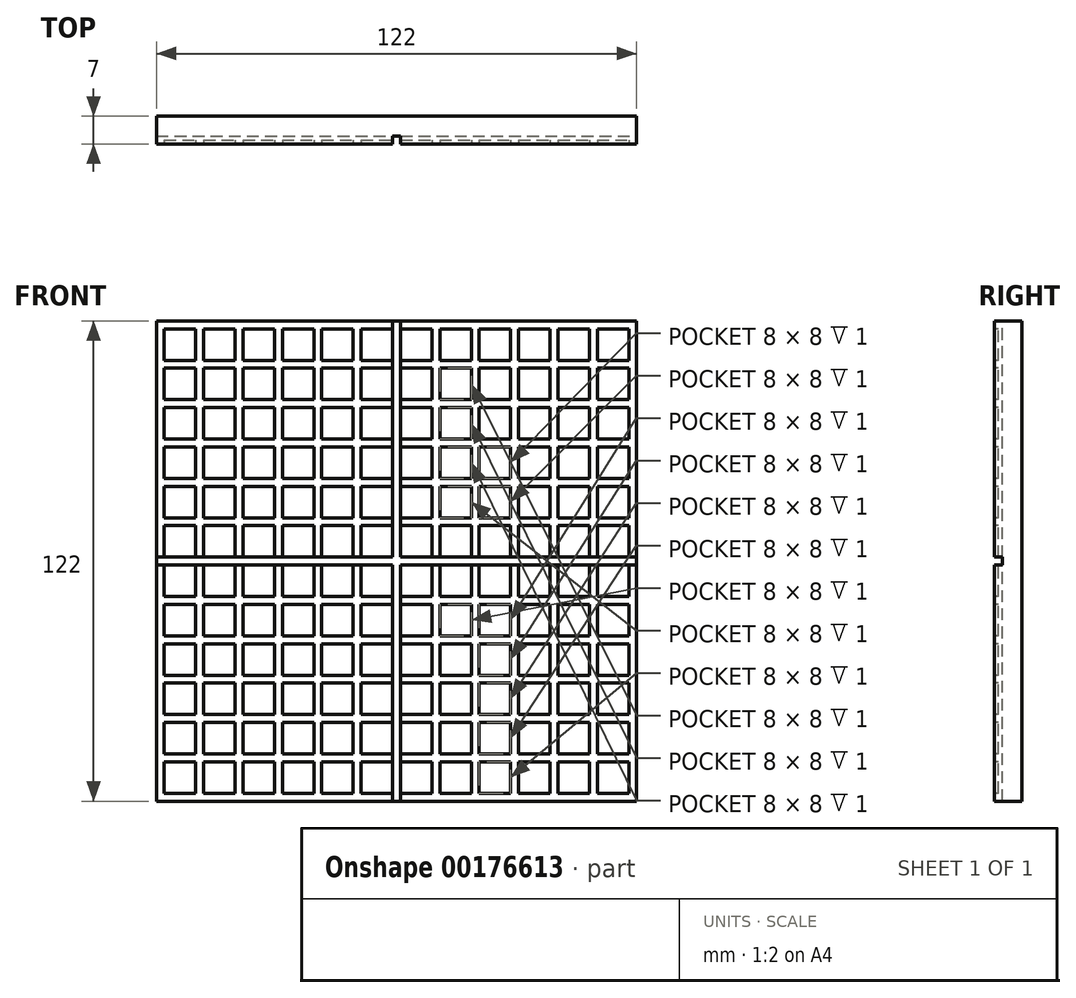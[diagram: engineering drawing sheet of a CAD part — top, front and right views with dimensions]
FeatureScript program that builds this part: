
annotation { "Feature Type Name" : "Feature", "Feature Type Description" : "" }
export const myFeature = defineFeature(function(context is Context, id is Id, definition is map)
    precondition{}
    {
        {
            var Q0;
            Q0=qCreatedBy(makeId("Front.planeOp"),FACE);
            var sketch = newSketch(context, id + "F0", { "sketchPlane" : qUnion([Q0])});
            skLineSegment(sketch, "E0.bottom", {"start": v(-61, 61) * mm, "end": v(61, 61) * mm});
            skLineSegment(sketch, "E0.top", {"start": v(-61, -61) * mm, "end": v(61, -61) * mm});
            skLineSegment(sketch, "E0.left", {"start": v(-61, 61) * mm, "end": v(-61, -61) * mm});
            skLineSegment(sketch, "E0.right", {"start": v(61, 61) * mm, "end": v(61, -61) * mm});
            skPoint(sketch, "E0.middle", {"position": v(0, 0) * mm});
            skSolve(sketch);
        }
        {
            var Q0;
            Q0=qCreatedBy(makeId("Front.planeOp"),FACE);
            var sketch = newSketch(context, id + "F1", { "sketchPlane" : qUnion([Q0])});
            skLineSegment(sketch, "E1.bottom", {"start": v(-61, 1) * mm, "end": v(61, 1) * mm});
            skLineSegment(sketch, "E1.top", {"start": v(-61, -1) * mm, "end": v(61, -1) * mm});
            skLineSegment(sketch, "E1.left", {"start": v(-61, 1) * mm, "end": v(-61, -1) * mm});
            skLineSegment(sketch, "E1.right", {"start": v(61, 1) * mm, "end": v(61, -1.62) * mm});
            skPoint(sketch, "E1.middle", {"position": v(0, 0) * mm});
            skLineSegment(sketch, "E2.bottom", {"start": v(-1, 61) * mm, "end": v(1, 61) * mm});
            skLineSegment(sketch, "E2.top", {"start": v(-1, -61) * mm, "end": v(1, -61) * mm});
            skLineSegment(sketch, "E2.left", {"start": v(-1, 61) * mm, "end": v(-1, -61) * mm});
            skLineSegment(sketch, "E2.right", {"start": v(1, 61) * mm, "end": v(1, -61) * mm});
            skSolve(sketch);
        }
        {
            var Q0;
            Q0=makeQuery(id+"F0.imprint","IMPRINT",FACE,{"disambiguationData":[TD([[makeQuery(id+"F0.imprint","IMPRINT",EDGE,{"derivedFrom":sQuery(id+"F0.wireOp",EDGE,"E0.bottom")}),-1.0]])]});
            var Q1;
            Q1 = qSketchRegion(id + "F4", true);
            extrude(context, id + "F2", {"entities" : qUnion([Q0, Q1]), "depth" : 7 * mm});
        }
        {
            var Q0;
            Q0 = qSketchRegion(id + "F1", true);
            extrude(context, id + "F3", {"entities" : qUnion([Q0]), "operationType" : NewBodyOperationType.ADD, "endBound" : BoundingType.UP_TO_NEXT, "depth" : 3 * mm, "offsetDistance" : 25 * mm});
        }
        {
            var Q0;
            {var subQ0=sQuery(id+"F1.wireOp",EDGE,"E1.left");var subQ1=sQuery(id+"F1.wireOp",EDGE,"E1.bottom");var subQ4=sQuery(id+"F0.wireOp",EDGE,"E0.left");var subQ5=sQuery(id+"F0.wireOp",EDGE,"E0.bottom");Q0=makeQuery(id+"F3.boolean.opBoolean","SPLIT",FACE,{"disambiguationData":[TD([makeQuery(id+"F3.opExtrude","SWEPT_FACE",FACE,{"disambiguationData":[OSD([subQ1]),TDD([makeQuery(id+"F1.imprint","IMPRINT",EDGE,{"disambiguationData":[TD([[makeQuery(id+"F1.imprint","INTERSECT",VERTEX,{"derivedFrom":[subQ1,subQ0]}),-1.0]])],"derivedFrom":subQ1})])]})])],"derivedFrom":makeQuery(id+"F2.opExtrude","CAP_FACE",FACE,{"disambiguationData":[OSD([subQ5,sQuery(id+"F0.wireOp",EDGE,"E0.top"),subQ4,sQuery(id+"F0.wireOp",EDGE,"E0.right")])],"isStart":false})});}
            var sketch = newSketch(context, id + "F4", { "sketchPlane" : qUnion([Q0])});
            skLineSegment(sketch, "E3.bottom", {"start": v(-59, -59) * mm, "end": v(-51, -59) * mm});
            skLineSegment(sketch, "E3.top", {"start": v(-59, -51) * mm, "end": v(-51, -51) * mm});
            skLineSegment(sketch, "E3.left", {"start": v(-59, -59) * mm, "end": v(-59, -51) * mm});
            skLineSegment(sketch, "E3.right", {"start": v(-51, -59) * mm, "end": v(-51, -51) * mm});
            skLineSegment(sketch, "E4.0.1.0", {"start": v(-51, -49) * mm, "end": v(-51, -41) * mm});
            skLineSegment(sketch, "E4.0.1.1", {"start": v(-59, -49) * mm, "end": v(-59, -41) * mm});
            skLineSegment(sketch, "E4.0.1.2", {"start": v(-59, -41) * mm, "end": v(-51, -41) * mm});
            skLineSegment(sketch, "E4.0.1.3", {"start": v(-59, -49) * mm, "end": v(-51, -49) * mm});
            skLineSegment(sketch, "E4.0.2.0", {"start": v(-51, -39) * mm, "end": v(-51, -31) * mm});
            skLineSegment(sketch, "E4.0.2.1", {"start": v(-59, -39) * mm, "end": v(-59, -31) * mm});
            skLineSegment(sketch, "E4.0.2.2", {"start": v(-59, -31) * mm, "end": v(-51, -31) * mm});
            skLineSegment(sketch, "E4.0.2.3", {"start": v(-59, -39) * mm, "end": v(-51, -39) * mm});
            skLineSegment(sketch, "E4.0.3.0", {"start": v(-51, -29) * mm, "end": v(-51, -21) * mm});
            skLineSegment(sketch, "E4.0.3.1", {"start": v(-59, -29) * mm, "end": v(-59, -21) * mm});
            skLineSegment(sketch, "E4.0.3.2", {"start": v(-59, -21) * mm, "end": v(-51, -21) * mm});
            skLineSegment(sketch, "E4.0.3.3", {"start": v(-59, -29) * mm, "end": v(-51, -29) * mm});
            skLineSegment(sketch, "E4.0.4.0", {"start": v(-51, -19) * mm, "end": v(-51, -11) * mm});
            skLineSegment(sketch, "E4.0.4.1", {"start": v(-59, -19) * mm, "end": v(-59, -11) * mm});
            skLineSegment(sketch, "E4.0.4.2", {"start": v(-59, -11) * mm, "end": v(-51, -11) * mm});
            skLineSegment(sketch, "E4.0.4.3", {"start": v(-59, -19) * mm, "end": v(-51, -19) * mm});
            skLineSegment(sketch, "E4.0.5.0", {"start": v(-51, -9) * mm, "end": v(-51, -1) * mm});
            skLineSegment(sketch, "E4.0.5.1", {"start": v(-59, -9) * mm, "end": v(-59, -1) * mm});
            skLineSegment(sketch, "E4.0.5.2", {"start": v(-59, -1) * mm, "end": v(-51, -1) * mm});
            skLineSegment(sketch, "E4.0.5.3", {"start": v(-59, -9) * mm, "end": v(-51, -9) * mm});
            skLineSegment(sketch, "E4.0.6.0", {"start": v(-51, 1) * mm, "end": v(-51, 9) * mm});
            skLineSegment(sketch, "E4.0.6.1", {"start": v(-59, 1) * mm, "end": v(-59, 9) * mm});
            skLineSegment(sketch, "E4.0.6.2", {"start": v(-59, 9) * mm, "end": v(-51, 9) * mm});
            skLineSegment(sketch, "E4.0.6.3", {"start": v(-59, 1) * mm, "end": v(-51, 1) * mm});
            skLineSegment(sketch, "E4.0.7.0", {"start": v(-51, 11) * mm, "end": v(-51, 19) * mm});
            skLineSegment(sketch, "E4.0.7.1", {"start": v(-59, 11) * mm, "end": v(-59, 19) * mm});
            skLineSegment(sketch, "E4.0.7.2", {"start": v(-59, 19) * mm, "end": v(-51, 19) * mm});
            skLineSegment(sketch, "E4.0.7.3", {"start": v(-59, 11) * mm, "end": v(-51, 11) * mm});
            skLineSegment(sketch, "E4.0.8.0", {"start": v(-51, 21) * mm, "end": v(-51, 29) * mm});
            skLineSegment(sketch, "E4.0.8.1", {"start": v(-59, 21) * mm, "end": v(-59, 29) * mm});
            skLineSegment(sketch, "E4.0.8.2", {"start": v(-59, 29) * mm, "end": v(-51, 29) * mm});
            skLineSegment(sketch, "E4.0.8.3", {"start": v(-59, 21) * mm, "end": v(-51, 21) * mm});
            skLineSegment(sketch, "E4.0.9.0", {"start": v(-51, 31) * mm, "end": v(-51, 39) * mm});
            skLineSegment(sketch, "E4.0.9.1", {"start": v(-59, 31) * mm, "end": v(-59, 39) * mm});
            skLineSegment(sketch, "E4.0.9.2", {"start": v(-59, 39) * mm, "end": v(-51, 39) * mm});
            skLineSegment(sketch, "E4.0.9.3", {"start": v(-59, 31) * mm, "end": v(-51, 31) * mm});
            skLineSegment(sketch, "E4.0.10.0", {"start": v(-51, 41) * mm, "end": v(-51, 49) * mm});
            skLineSegment(sketch, "E4.0.10.1", {"start": v(-59, 41) * mm, "end": v(-59, 49) * mm});
            skLineSegment(sketch, "E4.0.10.2", {"start": v(-59, 49) * mm, "end": v(-51, 49) * mm});
            skLineSegment(sketch, "E4.0.10.3", {"start": v(-59, 41) * mm, "end": v(-51, 41) * mm});
            skLineSegment(sketch, "E4.1.0.0", {"start": v(-41, -59) * mm, "end": v(-41, -51) * mm});
            skLineSegment(sketch, "E4.1.0.1", {"start": v(-49, -59) * mm, "end": v(-49, -51) * mm});
            skLineSegment(sketch, "E4.1.0.2", {"start": v(-49, -51) * mm, "end": v(-41, -51) * mm});
            skLineSegment(sketch, "E4.1.0.3", {"start": v(-49, -59) * mm, "end": v(-41, -59) * mm});
            skLineSegment(sketch, "E4.1.1.0", {"start": v(-41, -49) * mm, "end": v(-41, -41) * mm});
            skLineSegment(sketch, "E4.1.1.1", {"start": v(-49, -49) * mm, "end": v(-49, -41) * mm});
            skLineSegment(sketch, "E4.1.1.2", {"start": v(-49, -41) * mm, "end": v(-41, -41) * mm});
            skLineSegment(sketch, "E4.1.1.3", {"start": v(-49, -49) * mm, "end": v(-41, -49) * mm});
            skLineSegment(sketch, "E4.1.2.0", {"start": v(-41, -39) * mm, "end": v(-41, -31) * mm});
            skLineSegment(sketch, "E4.1.2.1", {"start": v(-49, -39) * mm, "end": v(-49, -31) * mm});
            skLineSegment(sketch, "E4.1.2.2", {"start": v(-49, -31) * mm, "end": v(-41, -31) * mm});
            skLineSegment(sketch, "E4.1.2.3", {"start": v(-49, -39) * mm, "end": v(-41, -39) * mm});
            skLineSegment(sketch, "E4.1.3.0", {"start": v(-41, -29) * mm, "end": v(-41, -21) * mm});
            skLineSegment(sketch, "E4.1.3.1", {"start": v(-49, -29) * mm, "end": v(-49, -21) * mm});
            skLineSegment(sketch, "E4.1.3.2", {"start": v(-49, -21) * mm, "end": v(-41, -21) * mm});
            skLineSegment(sketch, "E4.1.3.3", {"start": v(-49, -29) * mm, "end": v(-41, -29) * mm});
            skLineSegment(sketch, "E4.1.4.0", {"start": v(-41, -19) * mm, "end": v(-41, -11) * mm});
            skLineSegment(sketch, "E4.1.4.1", {"start": v(-49, -19) * mm, "end": v(-49, -11) * mm});
            skLineSegment(sketch, "E4.1.4.2", {"start": v(-49, -11) * mm, "end": v(-41, -11) * mm});
            skLineSegment(sketch, "E4.1.4.3", {"start": v(-49, -19) * mm, "end": v(-41, -19) * mm});
            skLineSegment(sketch, "E4.1.5.0", {"start": v(-41, -9) * mm, "end": v(-41, -1) * mm});
            skLineSegment(sketch, "E4.1.5.1", {"start": v(-49, -9) * mm, "end": v(-49, -1) * mm});
            skLineSegment(sketch, "E4.1.5.2", {"start": v(-49, -1) * mm, "end": v(-41, -1) * mm});
            skLineSegment(sketch, "E4.1.5.3", {"start": v(-49, -9) * mm, "end": v(-41, -9) * mm});
            skLineSegment(sketch, "E4.1.6.0", {"start": v(-41, 1) * mm, "end": v(-41, 9) * mm});
            skLineSegment(sketch, "E4.1.6.1", {"start": v(-49, 1) * mm, "end": v(-49, 9) * mm});
            skLineSegment(sketch, "E4.1.6.2", {"start": v(-49, 9) * mm, "end": v(-41, 9) * mm});
            skLineSegment(sketch, "E4.1.6.3", {"start": v(-49, 1) * mm, "end": v(-41, 1) * mm});
            skLineSegment(sketch, "E4.1.7.0", {"start": v(-41, 11) * mm, "end": v(-41, 19) * mm});
            skLineSegment(sketch, "E4.1.7.1", {"start": v(-49, 11) * mm, "end": v(-49, 19) * mm});
            skLineSegment(sketch, "E4.1.7.2", {"start": v(-49, 19) * mm, "end": v(-41, 19) * mm});
            skLineSegment(sketch, "E4.1.7.3", {"start": v(-49, 11) * mm, "end": v(-41, 11) * mm});
            skLineSegment(sketch, "E4.1.8.0", {"start": v(-41, 21) * mm, "end": v(-41, 29) * mm});
            skLineSegment(sketch, "E4.1.8.1", {"start": v(-49, 21) * mm, "end": v(-49, 29) * mm});
            skLineSegment(sketch, "E4.1.8.2", {"start": v(-49, 29) * mm, "end": v(-41, 29) * mm});
            skLineSegment(sketch, "E4.1.8.3", {"start": v(-49, 21) * mm, "end": v(-41, 21) * mm});
            skLineSegment(sketch, "E4.1.9.0", {"start": v(-41, 31) * mm, "end": v(-41, 39) * mm});
            skLineSegment(sketch, "E4.1.9.1", {"start": v(-49, 31) * mm, "end": v(-49, 39) * mm});
            skLineSegment(sketch, "E4.1.9.2", {"start": v(-49, 39) * mm, "end": v(-41, 39) * mm});
            skLineSegment(sketch, "E4.1.9.3", {"start": v(-49, 31) * mm, "end": v(-41, 31) * mm});
            skLineSegment(sketch, "E4.1.10.0", {"start": v(-41, 41) * mm, "end": v(-41, 49) * mm});
            skLineSegment(sketch, "E4.1.10.1", {"start": v(-49, 41) * mm, "end": v(-49, 49) * mm});
            skLineSegment(sketch, "E4.1.10.2", {"start": v(-49, 49) * mm, "end": v(-41, 49) * mm});
            skLineSegment(sketch, "E4.1.10.3", {"start": v(-49, 41) * mm, "end": v(-41, 41) * mm});
            skLineSegment(sketch, "E4.2.0.0", {"start": v(-31, -59) * mm, "end": v(-31, -51) * mm});
            skLineSegment(sketch, "E4.2.0.1", {"start": v(-39, -59) * mm, "end": v(-39, -51) * mm});
            skLineSegment(sketch, "E4.2.0.2", {"start": v(-39, -51) * mm, "end": v(-31, -51) * mm});
            skLineSegment(sketch, "E4.2.0.3", {"start": v(-39, -59) * mm, "end": v(-31, -59) * mm});
            skLineSegment(sketch, "E4.2.1.0", {"start": v(-31, -49) * mm, "end": v(-31, -41) * mm});
            skLineSegment(sketch, "E4.2.1.1", {"start": v(-39, -49) * mm, "end": v(-39, -41) * mm});
            skLineSegment(sketch, "E4.2.1.2", {"start": v(-39, -41) * mm, "end": v(-31, -41) * mm});
            skLineSegment(sketch, "E4.2.1.3", {"start": v(-39, -49) * mm, "end": v(-31, -49) * mm});
            skLineSegment(sketch, "E4.2.2.0", {"start": v(-31, -39) * mm, "end": v(-31, -31) * mm});
            skLineSegment(sketch, "E4.2.2.1", {"start": v(-39, -39) * mm, "end": v(-39, -31) * mm});
            skLineSegment(sketch, "E4.2.2.2", {"start": v(-39, -31) * mm, "end": v(-31, -31) * mm});
            skLineSegment(sketch, "E4.2.2.3", {"start": v(-39, -39) * mm, "end": v(-31, -39) * mm});
            skLineSegment(sketch, "E4.2.3.0", {"start": v(-31, -29) * mm, "end": v(-31, -21) * mm});
            skLineSegment(sketch, "E4.2.3.1", {"start": v(-39, -29) * mm, "end": v(-39, -21) * mm});
            skLineSegment(sketch, "E4.2.3.2", {"start": v(-39, -21) * mm, "end": v(-31, -21) * mm});
            skLineSegment(sketch, "E4.2.3.3", {"start": v(-39, -29) * mm, "end": v(-31, -29) * mm});
            skLineSegment(sketch, "E4.2.4.0", {"start": v(-31, -19) * mm, "end": v(-31, -11) * mm});
            skLineSegment(sketch, "E4.2.4.1", {"start": v(-39, -19) * mm, "end": v(-39, -11) * mm});
            skLineSegment(sketch, "E4.2.4.2", {"start": v(-39, -11) * mm, "end": v(-31, -11) * mm});
            skLineSegment(sketch, "E4.2.4.3", {"start": v(-39, -19) * mm, "end": v(-31, -19) * mm});
            skLineSegment(sketch, "E4.2.5.0", {"start": v(-31, -9) * mm, "end": v(-31, -1) * mm});
            skLineSegment(sketch, "E4.2.5.1", {"start": v(-39, -9) * mm, "end": v(-39, -1) * mm});
            skLineSegment(sketch, "E4.2.5.2", {"start": v(-39, -1) * mm, "end": v(-31, -1) * mm});
            skLineSegment(sketch, "E4.2.5.3", {"start": v(-39, -9) * mm, "end": v(-31, -9) * mm});
            skLineSegment(sketch, "E4.2.6.0", {"start": v(-31, 1) * mm, "end": v(-31, 9) * mm});
            skLineSegment(sketch, "E4.2.6.1", {"start": v(-39, 1) * mm, "end": v(-39, 9) * mm});
            skLineSegment(sketch, "E4.2.6.2", {"start": v(-39, 9) * mm, "end": v(-31, 9) * mm});
            skLineSegment(sketch, "E4.2.6.3", {"start": v(-39, 1) * mm, "end": v(-31, 1) * mm});
            skLineSegment(sketch, "E4.2.7.0", {"start": v(-31, 11) * mm, "end": v(-31, 19) * mm});
            skLineSegment(sketch, "E4.2.7.1", {"start": v(-39, 11) * mm, "end": v(-39, 19) * mm});
            skLineSegment(sketch, "E4.2.7.2", {"start": v(-39, 19) * mm, "end": v(-31, 19) * mm});
            skLineSegment(sketch, "E4.2.7.3", {"start": v(-39, 11) * mm, "end": v(-31, 11) * mm});
            skLineSegment(sketch, "E4.2.8.0", {"start": v(-31, 21) * mm, "end": v(-31, 29) * mm});
            skLineSegment(sketch, "E4.2.8.1", {"start": v(-39, 21) * mm, "end": v(-39, 29) * mm});
            skLineSegment(sketch, "E4.2.8.2", {"start": v(-39, 29) * mm, "end": v(-31, 29) * mm});
            skLineSegment(sketch, "E4.2.8.3", {"start": v(-39, 21) * mm, "end": v(-31, 21) * mm});
            skLineSegment(sketch, "E4.2.9.0", {"start": v(-31, 31) * mm, "end": v(-31, 39) * mm});
            skLineSegment(sketch, "E4.2.9.1", {"start": v(-39, 31) * mm, "end": v(-39, 39) * mm});
            skLineSegment(sketch, "E4.2.9.2", {"start": v(-39, 39) * mm, "end": v(-31, 39) * mm});
            skLineSegment(sketch, "E4.2.9.3", {"start": v(-39, 31) * mm, "end": v(-31, 31) * mm});
            skLineSegment(sketch, "E4.2.10.0", {"start": v(-31, 41) * mm, "end": v(-31, 49) * mm});
            skLineSegment(sketch, "E4.2.10.1", {"start": v(-39, 41) * mm, "end": v(-39, 49) * mm});
            skLineSegment(sketch, "E4.2.10.2", {"start": v(-39, 49) * mm, "end": v(-31, 49) * mm});
            skLineSegment(sketch, "E4.2.10.3", {"start": v(-39, 41) * mm, "end": v(-31, 41) * mm});
            skLineSegment(sketch, "E4.3.0.0", {"start": v(-21, -59) * mm, "end": v(-21, -51) * mm});
            skLineSegment(sketch, "E4.3.0.1", {"start": v(-29, -59) * mm, "end": v(-29, -51) * mm});
            skLineSegment(sketch, "E4.3.0.2", {"start": v(-29, -51) * mm, "end": v(-21, -51) * mm});
            skLineSegment(sketch, "E4.3.0.3", {"start": v(-29, -59) * mm, "end": v(-21, -59) * mm});
            skLineSegment(sketch, "E4.3.1.0", {"start": v(-21, -49) * mm, "end": v(-21, -41) * mm});
            skLineSegment(sketch, "E4.3.1.1", {"start": v(-29, -49) * mm, "end": v(-29, -41) * mm});
            skLineSegment(sketch, "E4.3.1.2", {"start": v(-29, -41) * mm, "end": v(-21, -41) * mm});
            skLineSegment(sketch, "E4.3.1.3", {"start": v(-29, -49) * mm, "end": v(-21, -49) * mm});
            skLineSegment(sketch, "E4.3.2.0", {"start": v(-21, -39) * mm, "end": v(-21, -31) * mm});
            skLineSegment(sketch, "E4.3.2.1", {"start": v(-29, -39) * mm, "end": v(-29, -31) * mm});
            skLineSegment(sketch, "E4.3.2.2", {"start": v(-29, -31) * mm, "end": v(-21, -31) * mm});
            skLineSegment(sketch, "E4.3.2.3", {"start": v(-29, -39) * mm, "end": v(-21, -39) * mm});
            skLineSegment(sketch, "E4.3.3.0", {"start": v(-21, -29) * mm, "end": v(-21, -21) * mm});
            skLineSegment(sketch, "E4.3.3.1", {"start": v(-29, -29) * mm, "end": v(-29, -21) * mm});
            skLineSegment(sketch, "E4.3.3.2", {"start": v(-29, -21) * mm, "end": v(-21, -21) * mm});
            skLineSegment(sketch, "E4.3.3.3", {"start": v(-29, -29) * mm, "end": v(-21, -29) * mm});
            skLineSegment(sketch, "E4.3.4.0", {"start": v(-21, -19) * mm, "end": v(-21, -11) * mm});
            skLineSegment(sketch, "E4.3.4.1", {"start": v(-29, -19) * mm, "end": v(-29, -11) * mm});
            skLineSegment(sketch, "E4.3.4.2", {"start": v(-29, -11) * mm, "end": v(-21, -11) * mm});
            skLineSegment(sketch, "E4.3.4.3", {"start": v(-29, -19) * mm, "end": v(-21, -19) * mm});
            skLineSegment(sketch, "E4.3.5.0", {"start": v(-21, -9) * mm, "end": v(-21, -1) * mm});
            skLineSegment(sketch, "E4.3.5.1", {"start": v(-29, -9) * mm, "end": v(-29, -1) * mm});
            skLineSegment(sketch, "E4.3.5.2", {"start": v(-29, -1) * mm, "end": v(-21, -1) * mm});
            skLineSegment(sketch, "E4.3.5.3", {"start": v(-29, -9) * mm, "end": v(-21, -9) * mm});
            skLineSegment(sketch, "E4.3.6.0", {"start": v(-21, 1) * mm, "end": v(-21, 9) * mm});
            skLineSegment(sketch, "E4.3.6.1", {"start": v(-29, 1) * mm, "end": v(-29, 9) * mm});
            skLineSegment(sketch, "E4.3.6.2", {"start": v(-29, 9) * mm, "end": v(-21, 9) * mm});
            skLineSegment(sketch, "E4.3.6.3", {"start": v(-29, 1) * mm, "end": v(-21, 1) * mm});
            skLineSegment(sketch, "E4.3.7.0", {"start": v(-21, 11) * mm, "end": v(-21, 19) * mm});
            skLineSegment(sketch, "E4.3.7.1", {"start": v(-29, 11) * mm, "end": v(-29, 19) * mm});
            skLineSegment(sketch, "E4.3.7.2", {"start": v(-29, 19) * mm, "end": v(-21, 19) * mm});
            skLineSegment(sketch, "E4.3.7.3", {"start": v(-29, 11) * mm, "end": v(-21, 11) * mm});
            skLineSegment(sketch, "E4.3.8.0", {"start": v(-21, 21) * mm, "end": v(-21, 29) * mm});
            skLineSegment(sketch, "E4.3.8.1", {"start": v(-29, 21) * mm, "end": v(-29, 29) * mm});
            skLineSegment(sketch, "E4.3.8.2", {"start": v(-29, 29) * mm, "end": v(-21, 29) * mm});
            skLineSegment(sketch, "E4.3.8.3", {"start": v(-29, 21) * mm, "end": v(-21, 21) * mm});
            skLineSegment(sketch, "E4.3.9.0", {"start": v(-21, 31) * mm, "end": v(-21, 39) * mm});
            skLineSegment(sketch, "E4.3.9.1", {"start": v(-29, 31) * mm, "end": v(-29, 39) * mm});
            skLineSegment(sketch, "E4.3.9.2", {"start": v(-29, 39) * mm, "end": v(-21, 39) * mm});
            skLineSegment(sketch, "E4.3.9.3", {"start": v(-29, 31) * mm, "end": v(-21, 31) * mm});
            skLineSegment(sketch, "E4.3.10.0", {"start": v(-21, 41) * mm, "end": v(-21, 49) * mm});
            skLineSegment(sketch, "E4.3.10.1", {"start": v(-29, 41) * mm, "end": v(-29, 49) * mm});
            skLineSegment(sketch, "E4.3.10.2", {"start": v(-29, 49) * mm, "end": v(-21, 49) * mm});
            skLineSegment(sketch, "E4.3.10.3", {"start": v(-29, 41) * mm, "end": v(-21, 41) * mm});
            skLineSegment(sketch, "E4.4.0.0", {"start": v(-11, -59) * mm, "end": v(-11, -51) * mm});
            skLineSegment(sketch, "E4.4.0.1", {"start": v(-19, -59) * mm, "end": v(-19, -51) * mm});
            skLineSegment(sketch, "E4.4.0.2", {"start": v(-19, -51) * mm, "end": v(-11, -51) * mm});
            skLineSegment(sketch, "E4.4.0.3", {"start": v(-19, -59) * mm, "end": v(-11, -59) * mm});
            skLineSegment(sketch, "E4.4.1.0", {"start": v(-11, -49) * mm, "end": v(-11, -41) * mm});
            skLineSegment(sketch, "E4.4.1.1", {"start": v(-19, -49) * mm, "end": v(-19, -41) * mm});
            skLineSegment(sketch, "E4.4.1.2", {"start": v(-19, -41) * mm, "end": v(-11, -41) * mm});
            skLineSegment(sketch, "E4.4.1.3", {"start": v(-19, -49) * mm, "end": v(-11, -49) * mm});
            skLineSegment(sketch, "E4.4.2.0", {"start": v(-11, -39) * mm, "end": v(-11, -31) * mm});
            skLineSegment(sketch, "E4.4.2.1", {"start": v(-19, -39) * mm, "end": v(-19, -31) * mm});
            skLineSegment(sketch, "E4.4.2.2", {"start": v(-19, -31) * mm, "end": v(-11, -31) * mm});
            skLineSegment(sketch, "E4.4.2.3", {"start": v(-19, -39) * mm, "end": v(-11, -39) * mm});
            skLineSegment(sketch, "E4.4.3.0", {"start": v(-11, -29) * mm, "end": v(-11, -21) * mm});
            skLineSegment(sketch, "E4.4.3.1", {"start": v(-19, -29) * mm, "end": v(-19, -21) * mm});
            skLineSegment(sketch, "E4.4.3.2", {"start": v(-19, -21) * mm, "end": v(-11, -21) * mm});
            skLineSegment(sketch, "E4.4.3.3", {"start": v(-19, -29) * mm, "end": v(-11, -29) * mm});
            skLineSegment(sketch, "E4.4.4.0", {"start": v(-11, -19) * mm, "end": v(-11, -11) * mm});
            skLineSegment(sketch, "E4.4.4.1", {"start": v(-19, -19) * mm, "end": v(-19, -11) * mm});
            skLineSegment(sketch, "E4.4.4.2", {"start": v(-19, -11) * mm, "end": v(-11, -11) * mm});
            skLineSegment(sketch, "E4.4.4.3", {"start": v(-19, -19) * mm, "end": v(-11, -19) * mm});
            skLineSegment(sketch, "E4.4.5.0", {"start": v(-11, -9) * mm, "end": v(-11, -1) * mm});
            skLineSegment(sketch, "E4.4.5.1", {"start": v(-19, -9) * mm, "end": v(-19, -1) * mm});
            skLineSegment(sketch, "E4.4.5.2", {"start": v(-19, -1) * mm, "end": v(-11, -1) * mm});
            skLineSegment(sketch, "E4.4.5.3", {"start": v(-19, -9) * mm, "end": v(-11, -9) * mm});
            skLineSegment(sketch, "E4.4.6.0", {"start": v(-11, 1) * mm, "end": v(-11, 9) * mm});
            skLineSegment(sketch, "E4.4.6.1", {"start": v(-19, 1) * mm, "end": v(-19, 9) * mm});
            skLineSegment(sketch, "E4.4.6.2", {"start": v(-19, 9) * mm, "end": v(-11, 9) * mm});
            skLineSegment(sketch, "E4.4.6.3", {"start": v(-19, 1) * mm, "end": v(-11, 1) * mm});
            skLineSegment(sketch, "E4.4.7.0", {"start": v(-11, 11) * mm, "end": v(-11, 19) * mm});
            skLineSegment(sketch, "E4.4.7.1", {"start": v(-19, 11) * mm, "end": v(-19, 19) * mm});
            skLineSegment(sketch, "E4.4.7.2", {"start": v(-19, 19) * mm, "end": v(-11, 19) * mm});
            skLineSegment(sketch, "E4.4.7.3", {"start": v(-19, 11) * mm, "end": v(-11, 11) * mm});
            skLineSegment(sketch, "E4.4.8.0", {"start": v(-11, 21) * mm, "end": v(-11, 29) * mm});
            skLineSegment(sketch, "E4.4.8.1", {"start": v(-19, 21) * mm, "end": v(-19, 29) * mm});
            skLineSegment(sketch, "E4.4.8.2", {"start": v(-19, 29) * mm, "end": v(-11, 29) * mm});
            skLineSegment(sketch, "E4.4.8.3", {"start": v(-19, 21) * mm, "end": v(-11, 21) * mm});
            skLineSegment(sketch, "E4.4.9.0", {"start": v(-11, 31) * mm, "end": v(-11, 39) * mm});
            skLineSegment(sketch, "E4.4.9.1", {"start": v(-19, 31) * mm, "end": v(-19, 39) * mm});
            skLineSegment(sketch, "E4.4.9.2", {"start": v(-19, 39) * mm, "end": v(-11, 39) * mm});
            skLineSegment(sketch, "E4.4.9.3", {"start": v(-19, 31) * mm, "end": v(-11, 31) * mm});
            skLineSegment(sketch, "E4.4.10.0", {"start": v(-11, 41) * mm, "end": v(-11, 49) * mm});
            skLineSegment(sketch, "E4.4.10.1", {"start": v(-19, 41) * mm, "end": v(-19, 49) * mm});
            skLineSegment(sketch, "E4.4.10.2", {"start": v(-19, 49) * mm, "end": v(-11, 49) * mm});
            skLineSegment(sketch, "E4.4.10.3", {"start": v(-19, 41) * mm, "end": v(-11, 41) * mm});
            skLineSegment(sketch, "E4.5.0.0", {"start": v(-1, -59) * mm, "end": v(-1, -51) * mm});
            skLineSegment(sketch, "E4.5.0.1", {"start": v(-9, -59) * mm, "end": v(-9, -51) * mm});
            skLineSegment(sketch, "E4.5.0.2", {"start": v(-9, -51) * mm, "end": v(-1, -51) * mm});
            skLineSegment(sketch, "E4.5.0.3", {"start": v(-9, -59) * mm, "end": v(-1, -59) * mm});
            skLineSegment(sketch, "E4.5.1.0", {"start": v(-1, -49) * mm, "end": v(-1, -41) * mm});
            skLineSegment(sketch, "E4.5.1.1", {"start": v(-9, -49) * mm, "end": v(-9, -41) * mm});
            skLineSegment(sketch, "E4.5.1.2", {"start": v(-9, -41) * mm, "end": v(-1, -41) * mm});
            skLineSegment(sketch, "E4.5.1.3", {"start": v(-9, -49) * mm, "end": v(-1, -49) * mm});
            skLineSegment(sketch, "E4.5.2.0", {"start": v(-1, -39) * mm, "end": v(-1, -31) * mm});
            skLineSegment(sketch, "E4.5.2.1", {"start": v(-9, -39) * mm, "end": v(-9, -31) * mm});
            skLineSegment(sketch, "E4.5.2.2", {"start": v(-9, -31) * mm, "end": v(-1, -31) * mm});
            skLineSegment(sketch, "E4.5.2.3", {"start": v(-9, -39) * mm, "end": v(-1, -39) * mm});
            skLineSegment(sketch, "E4.5.3.0", {"start": v(-1, -29) * mm, "end": v(-1, -21) * mm});
            skLineSegment(sketch, "E4.5.3.1", {"start": v(-9, -29) * mm, "end": v(-9, -21) * mm});
            skLineSegment(sketch, "E4.5.3.2", {"start": v(-9, -21) * mm, "end": v(-1, -21) * mm});
            skLineSegment(sketch, "E4.5.3.3", {"start": v(-9, -29) * mm, "end": v(-1, -29) * mm});
            skLineSegment(sketch, "E4.5.4.0", {"start": v(-1, -19) * mm, "end": v(-1, -11) * mm});
            skLineSegment(sketch, "E4.5.4.1", {"start": v(-9, -19) * mm, "end": v(-9, -11) * mm});
            skLineSegment(sketch, "E4.5.4.2", {"start": v(-9, -11) * mm, "end": v(-1, -11) * mm});
            skLineSegment(sketch, "E4.5.4.3", {"start": v(-9, -19) * mm, "end": v(-1, -19) * mm});
            skLineSegment(sketch, "E4.5.5.0", {"start": v(-1, -9) * mm, "end": v(-1, -1) * mm});
            skLineSegment(sketch, "E4.5.5.1", {"start": v(-9, -9) * mm, "end": v(-9, -1) * mm});
            skLineSegment(sketch, "E4.5.5.2", {"start": v(-9, -1) * mm, "end": v(-1, -1) * mm});
            skLineSegment(sketch, "E4.5.5.3", {"start": v(-9, -9) * mm, "end": v(-1, -9) * mm});
            skLineSegment(sketch, "E4.5.6.0", {"start": v(-1, 1) * mm, "end": v(-1, 9) * mm});
            skLineSegment(sketch, "E4.5.6.1", {"start": v(-9, 1) * mm, "end": v(-9, 9) * mm});
            skLineSegment(sketch, "E4.5.6.2", {"start": v(-9, 9) * mm, "end": v(-1, 9) * mm});
            skLineSegment(sketch, "E4.5.6.3", {"start": v(-9, 1) * mm, "end": v(-1, 1) * mm});
            skLineSegment(sketch, "E4.5.7.0", {"start": v(-1, 11) * mm, "end": v(-1, 19) * mm});
            skLineSegment(sketch, "E4.5.7.1", {"start": v(-9, 11) * mm, "end": v(-9, 19) * mm});
            skLineSegment(sketch, "E4.5.7.2", {"start": v(-9, 19) * mm, "end": v(-1, 19) * mm});
            skLineSegment(sketch, "E4.5.7.3", {"start": v(-9, 11) * mm, "end": v(-1, 11) * mm});
            skLineSegment(sketch, "E4.5.8.0", {"start": v(-1, 21) * mm, "end": v(-1, 29) * mm});
            skLineSegment(sketch, "E4.5.8.1", {"start": v(-9, 21) * mm, "end": v(-9, 29) * mm});
            skLineSegment(sketch, "E4.5.8.2", {"start": v(-9, 29) * mm, "end": v(-1, 29) * mm});
            skLineSegment(sketch, "E4.5.8.3", {"start": v(-9, 21) * mm, "end": v(-1, 21) * mm});
            skLineSegment(sketch, "E4.5.9.0", {"start": v(-1, 31) * mm, "end": v(-1, 39) * mm});
            skLineSegment(sketch, "E4.5.9.1", {"start": v(-9, 31) * mm, "end": v(-9, 39) * mm});
            skLineSegment(sketch, "E4.5.9.2", {"start": v(-9, 39) * mm, "end": v(-1, 39) * mm});
            skLineSegment(sketch, "E4.5.9.3", {"start": v(-9, 31) * mm, "end": v(-1, 31) * mm});
            skLineSegment(sketch, "E4.5.10.0", {"start": v(-1, 41) * mm, "end": v(-1, 49) * mm});
            skLineSegment(sketch, "E4.5.10.1", {"start": v(-9, 41) * mm, "end": v(-9, 49) * mm});
            skLineSegment(sketch, "E4.5.10.2", {"start": v(-9, 49) * mm, "end": v(-1, 49) * mm});
            skLineSegment(sketch, "E4.5.10.3", {"start": v(-9, 41) * mm, "end": v(-1, 41) * mm});
            skLineSegment(sketch, "E4.6.0.0", {"start": v(9, -59) * mm, "end": v(9, -51) * mm});
            skLineSegment(sketch, "E4.6.0.1", {"start": v(1, -59) * mm, "end": v(1, -51) * mm});
            skLineSegment(sketch, "E4.6.0.2", {"start": v(1, -51) * mm, "end": v(9, -51) * mm});
            skLineSegment(sketch, "E4.6.0.3", {"start": v(1, -59) * mm, "end": v(9, -59) * mm});
            skLineSegment(sketch, "E4.6.1.0", {"start": v(9, -49) * mm, "end": v(9, -41) * mm});
            skLineSegment(sketch, "E4.6.1.1", {"start": v(1, -49) * mm, "end": v(1, -41) * mm});
            skLineSegment(sketch, "E4.6.1.2", {"start": v(1, -41) * mm, "end": v(9, -41) * mm});
            skLineSegment(sketch, "E4.6.1.3", {"start": v(1, -49) * mm, "end": v(9, -49) * mm});
            skLineSegment(sketch, "E4.6.2.0", {"start": v(9, -39) * mm, "end": v(9, -31) * mm});
            skLineSegment(sketch, "E4.6.2.1", {"start": v(1, -39) * mm, "end": v(1, -31) * mm});
            skLineSegment(sketch, "E4.6.2.2", {"start": v(1, -31) * mm, "end": v(9, -31) * mm});
            skLineSegment(sketch, "E4.6.2.3", {"start": v(1, -39) * mm, "end": v(9, -39) * mm});
            skLineSegment(sketch, "E4.6.3.0", {"start": v(9, -29) * mm, "end": v(9, -21) * mm});
            skLineSegment(sketch, "E4.6.3.1", {"start": v(1, -29) * mm, "end": v(1, -21) * mm});
            skLineSegment(sketch, "E4.6.3.2", {"start": v(1, -21) * mm, "end": v(9, -21) * mm});
            skLineSegment(sketch, "E4.6.3.3", {"start": v(1, -29) * mm, "end": v(9, -29) * mm});
            skLineSegment(sketch, "E4.6.4.0", {"start": v(9, -19) * mm, "end": v(9, -11) * mm});
            skLineSegment(sketch, "E4.6.4.1", {"start": v(1, -19) * mm, "end": v(1, -11) * mm});
            skLineSegment(sketch, "E4.6.4.2", {"start": v(1, -11) * mm, "end": v(9, -11) * mm});
            skLineSegment(sketch, "E4.6.4.3", {"start": v(1, -19) * mm, "end": v(9, -19) * mm});
            skLineSegment(sketch, "E4.6.5.0", {"start": v(9, -9) * mm, "end": v(9, -1) * mm});
            skLineSegment(sketch, "E4.6.5.1", {"start": v(1, -9) * mm, "end": v(1, -1) * mm});
            skLineSegment(sketch, "E4.6.5.2", {"start": v(1, -1) * mm, "end": v(9, -1) * mm});
            skLineSegment(sketch, "E4.6.5.3", {"start": v(1, -9) * mm, "end": v(9, -9) * mm});
            skLineSegment(sketch, "E4.6.6.0", {"start": v(9, 1) * mm, "end": v(9, 9) * mm});
            skLineSegment(sketch, "E4.6.6.1", {"start": v(1, 1) * mm, "end": v(1, 9) * mm});
            skLineSegment(sketch, "E4.6.6.2", {"start": v(1, 9) * mm, "end": v(9, 9) * mm});
            skLineSegment(sketch, "E4.6.6.3", {"start": v(1, 1) * mm, "end": v(9, 1) * mm});
            skLineSegment(sketch, "E4.6.7.0", {"start": v(9, 11) * mm, "end": v(9, 19) * mm});
            skLineSegment(sketch, "E4.6.7.1", {"start": v(1, 11) * mm, "end": v(1, 19) * mm});
            skLineSegment(sketch, "E4.6.7.2", {"start": v(1, 19) * mm, "end": v(9, 19) * mm});
            skLineSegment(sketch, "E4.6.7.3", {"start": v(1, 11) * mm, "end": v(9, 11) * mm});
            skLineSegment(sketch, "E4.6.8.0", {"start": v(9, 21) * mm, "end": v(9, 29) * mm});
            skLineSegment(sketch, "E4.6.8.1", {"start": v(1, 21) * mm, "end": v(1, 29) * mm});
            skLineSegment(sketch, "E4.6.8.2", {"start": v(1, 29) * mm, "end": v(9, 29) * mm});
            skLineSegment(sketch, "E4.6.8.3", {"start": v(1, 21) * mm, "end": v(9, 21) * mm});
            skLineSegment(sketch, "E4.6.9.0", {"start": v(9, 31) * mm, "end": v(9, 39) * mm});
            skLineSegment(sketch, "E4.6.9.1", {"start": v(1, 31) * mm, "end": v(1, 39) * mm});
            skLineSegment(sketch, "E4.6.9.2", {"start": v(1, 39) * mm, "end": v(9, 39) * mm});
            skLineSegment(sketch, "E4.6.9.3", {"start": v(1, 31) * mm, "end": v(9, 31) * mm});
            skLineSegment(sketch, "E4.6.10.0", {"start": v(9, 41) * mm, "end": v(9, 49) * mm});
            skLineSegment(sketch, "E4.6.10.1", {"start": v(1, 41) * mm, "end": v(1, 49) * mm});
            skLineSegment(sketch, "E4.6.10.2", {"start": v(1, 49) * mm, "end": v(9, 49) * mm});
            skLineSegment(sketch, "E4.6.10.3", {"start": v(1, 41) * mm, "end": v(9, 41) * mm});
            skLineSegment(sketch, "E4.7.0.0", {"start": v(19, -59) * mm, "end": v(19, -51) * mm});
            skLineSegment(sketch, "E4.7.0.1", {"start": v(11, -59) * mm, "end": v(11, -51) * mm});
            skLineSegment(sketch, "E4.7.0.2", {"start": v(11, -51) * mm, "end": v(19, -51) * mm});
            skLineSegment(sketch, "E4.7.0.3", {"start": v(11, -59) * mm, "end": v(19, -59) * mm});
            skLineSegment(sketch, "E4.7.1.0", {"start": v(19, -49) * mm, "end": v(19, -41) * mm});
            skLineSegment(sketch, "E4.7.1.1", {"start": v(11, -49) * mm, "end": v(11, -41) * mm});
            skLineSegment(sketch, "E4.7.1.2", {"start": v(11, -41) * mm, "end": v(19, -41) * mm});
            skLineSegment(sketch, "E4.7.1.3", {"start": v(11, -49) * mm, "end": v(19, -49) * mm});
            skLineSegment(sketch, "E4.7.2.0", {"start": v(19, -39) * mm, "end": v(19, -31) * mm});
            skLineSegment(sketch, "E4.7.2.1", {"start": v(11, -39) * mm, "end": v(11, -31) * mm});
            skLineSegment(sketch, "E4.7.2.2", {"start": v(11, -31) * mm, "end": v(19, -31) * mm});
            skLineSegment(sketch, "E4.7.2.3", {"start": v(11, -39) * mm, "end": v(19, -39) * mm});
            skLineSegment(sketch, "E4.7.3.0", {"start": v(19, -29) * mm, "end": v(19, -21) * mm});
            skLineSegment(sketch, "E4.7.3.1", {"start": v(11, -29) * mm, "end": v(11, -21) * mm});
            skLineSegment(sketch, "E4.7.3.2", {"start": v(11, -21) * mm, "end": v(19, -21) * mm});
            skLineSegment(sketch, "E4.7.3.3", {"start": v(11, -29) * mm, "end": v(19, -29) * mm});
            skLineSegment(sketch, "E4.7.4.0", {"start": v(19, -19) * mm, "end": v(19, -11) * mm});
            skLineSegment(sketch, "E4.7.4.1", {"start": v(11, -19) * mm, "end": v(11, -11) * mm});
            skLineSegment(sketch, "E4.7.4.2", {"start": v(11, -11) * mm, "end": v(19, -11) * mm});
            skLineSegment(sketch, "E4.7.4.3", {"start": v(11, -19) * mm, "end": v(19, -19) * mm});
            skLineSegment(sketch, "E4.7.5.0", {"start": v(19, -9) * mm, "end": v(19, -1) * mm});
            skLineSegment(sketch, "E4.7.5.1", {"start": v(11, -9) * mm, "end": v(11, -1) * mm});
            skLineSegment(sketch, "E4.7.5.2", {"start": v(11, -1) * mm, "end": v(19, -1) * mm});
            skLineSegment(sketch, "E4.7.5.3", {"start": v(11, -9) * mm, "end": v(19, -9) * mm});
            skLineSegment(sketch, "E4.7.6.0", {"start": v(19, 1) * mm, "end": v(19, 9) * mm});
            skLineSegment(sketch, "E4.7.6.1", {"start": v(11, 1) * mm, "end": v(11, 9) * mm});
            skLineSegment(sketch, "E4.7.6.2", {"start": v(11, 9) * mm, "end": v(19, 9) * mm});
            skLineSegment(sketch, "E4.7.6.3", {"start": v(11, 1) * mm, "end": v(19, 1) * mm});
            skLineSegment(sketch, "E4.7.7.0", {"start": v(19, 11) * mm, "end": v(19, 19) * mm});
            skLineSegment(sketch, "E4.7.7.1", {"start": v(11, 11) * mm, "end": v(11, 19) * mm});
            skLineSegment(sketch, "E4.7.7.2", {"start": v(11, 19) * mm, "end": v(19, 19) * mm});
            skLineSegment(sketch, "E4.7.7.3", {"start": v(11, 11) * mm, "end": v(19, 11) * mm});
            skLineSegment(sketch, "E4.7.8.0", {"start": v(19, 21) * mm, "end": v(19, 29) * mm});
            skLineSegment(sketch, "E4.7.8.1", {"start": v(11, 21) * mm, "end": v(11, 29) * mm});
            skLineSegment(sketch, "E4.7.8.2", {"start": v(11, 29) * mm, "end": v(19, 29) * mm});
            skLineSegment(sketch, "E4.7.8.3", {"start": v(11, 21) * mm, "end": v(19, 21) * mm});
            skLineSegment(sketch, "E4.7.9.0", {"start": v(19, 31) * mm, "end": v(19, 39) * mm});
            skLineSegment(sketch, "E4.7.9.1", {"start": v(11, 31) * mm, "end": v(11, 39) * mm});
            skLineSegment(sketch, "E4.7.9.2", {"start": v(11, 39) * mm, "end": v(19, 39) * mm});
            skLineSegment(sketch, "E4.7.9.3", {"start": v(11, 31) * mm, "end": v(19, 31) * mm});
            skLineSegment(sketch, "E4.7.10.0", {"start": v(19, 41) * mm, "end": v(19, 49) * mm});
            skLineSegment(sketch, "E4.7.10.1", {"start": v(11, 41) * mm, "end": v(11, 49) * mm});
            skLineSegment(sketch, "E4.7.10.2", {"start": v(11, 49) * mm, "end": v(19, 49) * mm});
            skLineSegment(sketch, "E4.7.10.3", {"start": v(11, 41) * mm, "end": v(19, 41) * mm});
            skLineSegment(sketch, "E4.8.0.0", {"start": v(29, -59) * mm, "end": v(29, -51) * mm});
            skLineSegment(sketch, "E4.8.0.1", {"start": v(21, -59) * mm, "end": v(21, -51) * mm});
            skLineSegment(sketch, "E4.8.0.2", {"start": v(21, -51) * mm, "end": v(29, -51) * mm});
            skLineSegment(sketch, "E4.8.0.3", {"start": v(21, -59) * mm, "end": v(29, -59) * mm});
            skLineSegment(sketch, "E4.8.1.0", {"start": v(29, -49) * mm, "end": v(29, -41) * mm});
            skLineSegment(sketch, "E4.8.1.1", {"start": v(21, -49) * mm, "end": v(21, -41) * mm});
            skLineSegment(sketch, "E4.8.1.2", {"start": v(21, -41) * mm, "end": v(29, -41) * mm});
            skLineSegment(sketch, "E4.8.1.3", {"start": v(21, -49) * mm, "end": v(29, -49) * mm});
            skLineSegment(sketch, "E4.8.2.0", {"start": v(29, -39) * mm, "end": v(29, -31) * mm});
            skLineSegment(sketch, "E4.8.2.1", {"start": v(21, -39) * mm, "end": v(21, -31) * mm});
            skLineSegment(sketch, "E4.8.2.2", {"start": v(21, -31) * mm, "end": v(29, -31) * mm});
            skLineSegment(sketch, "E4.8.2.3", {"start": v(21, -39) * mm, "end": v(29, -39) * mm});
            skLineSegment(sketch, "E4.8.3.0", {"start": v(29, -29) * mm, "end": v(29, -21) * mm});
            skLineSegment(sketch, "E4.8.3.1", {"start": v(21, -29) * mm, "end": v(21, -21) * mm});
            skLineSegment(sketch, "E4.8.3.2", {"start": v(21, -21) * mm, "end": v(29, -21) * mm});
            skLineSegment(sketch, "E4.8.3.3", {"start": v(21, -29) * mm, "end": v(29, -29) * mm});
            skLineSegment(sketch, "E4.8.4.0", {"start": v(29, -19) * mm, "end": v(29, -11) * mm});
            skLineSegment(sketch, "E4.8.4.1", {"start": v(21, -19) * mm, "end": v(21, -11) * mm});
            skLineSegment(sketch, "E4.8.4.2", {"start": v(21, -11) * mm, "end": v(29, -11) * mm});
            skLineSegment(sketch, "E4.8.4.3", {"start": v(21, -19) * mm, "end": v(29, -19) * mm});
            skLineSegment(sketch, "E4.8.5.0", {"start": v(29, -9) * mm, "end": v(29, -1) * mm});
            skLineSegment(sketch, "E4.8.5.1", {"start": v(21, -9) * mm, "end": v(21, -1) * mm});
            skLineSegment(sketch, "E4.8.5.2", {"start": v(21, -1) * mm, "end": v(29, -1) * mm});
            skLineSegment(sketch, "E4.8.5.3", {"start": v(21, -9) * mm, "end": v(29, -9) * mm});
            skLineSegment(sketch, "E4.8.6.0", {"start": v(29, 1) * mm, "end": v(29, 9) * mm});
            skLineSegment(sketch, "E4.8.6.1", {"start": v(21, 1) * mm, "end": v(21, 9) * mm});
            skLineSegment(sketch, "E4.8.6.2", {"start": v(21, 9) * mm, "end": v(29, 9) * mm});
            skLineSegment(sketch, "E4.8.6.3", {"start": v(21, 1) * mm, "end": v(29, 1) * mm});
            skLineSegment(sketch, "E4.8.7.0", {"start": v(29, 11) * mm, "end": v(29, 19) * mm});
            skLineSegment(sketch, "E4.8.7.1", {"start": v(21, 11) * mm, "end": v(21, 19) * mm});
            skLineSegment(sketch, "E4.8.7.2", {"start": v(21, 19) * mm, "end": v(29, 19) * mm});
            skLineSegment(sketch, "E4.8.7.3", {"start": v(21, 11) * mm, "end": v(29, 11) * mm});
            skLineSegment(sketch, "E4.8.8.0", {"start": v(29, 21) * mm, "end": v(29, 29) * mm});
            skLineSegment(sketch, "E4.8.8.1", {"start": v(21, 21) * mm, "end": v(21, 29) * mm});
            skLineSegment(sketch, "E4.8.8.2", {"start": v(21, 29) * mm, "end": v(29, 29) * mm});
            skLineSegment(sketch, "E4.8.8.3", {"start": v(21, 21) * mm, "end": v(29, 21) * mm});
            skLineSegment(sketch, "E4.8.9.0", {"start": v(29, 31) * mm, "end": v(29, 39) * mm});
            skLineSegment(sketch, "E4.8.9.1", {"start": v(21, 31) * mm, "end": v(21, 39) * mm});
            skLineSegment(sketch, "E4.8.9.2", {"start": v(21, 39) * mm, "end": v(29, 39) * mm});
            skLineSegment(sketch, "E4.8.9.3", {"start": v(21, 31) * mm, "end": v(29, 31) * mm});
            skLineSegment(sketch, "E4.8.10.0", {"start": v(29, 41) * mm, "end": v(29, 49) * mm});
            skLineSegment(sketch, "E4.8.10.1", {"start": v(21, 41) * mm, "end": v(21, 49) * mm});
            skLineSegment(sketch, "E4.8.10.2", {"start": v(21, 49) * mm, "end": v(29, 49) * mm});
            skLineSegment(sketch, "E4.8.10.3", {"start": v(21, 41) * mm, "end": v(29, 41) * mm});
            skLineSegment(sketch, "E4.9.0.0", {"start": v(39, -59) * mm, "end": v(39, -51) * mm});
            skLineSegment(sketch, "E4.9.0.1", {"start": v(31, -59) * mm, "end": v(31, -51) * mm});
            skLineSegment(sketch, "E4.9.0.2", {"start": v(31, -51) * mm, "end": v(39, -51) * mm});
            skLineSegment(sketch, "E4.9.0.3", {"start": v(31, -59) * mm, "end": v(39, -59) * mm});
            skLineSegment(sketch, "E4.9.1.0", {"start": v(39, -49) * mm, "end": v(39, -41) * mm});
            skLineSegment(sketch, "E4.9.1.1", {"start": v(31, -49) * mm, "end": v(31, -41) * mm});
            skLineSegment(sketch, "E4.9.1.2", {"start": v(31, -41) * mm, "end": v(39, -41) * mm});
            skLineSegment(sketch, "E4.9.1.3", {"start": v(31, -49) * mm, "end": v(39, -49) * mm});
            skLineSegment(sketch, "E4.9.2.0", {"start": v(39, -39) * mm, "end": v(39, -31) * mm});
            skLineSegment(sketch, "E4.9.2.1", {"start": v(31, -39) * mm, "end": v(31, -31) * mm});
            skLineSegment(sketch, "E4.9.2.2", {"start": v(31, -31) * mm, "end": v(39, -31) * mm});
            skLineSegment(sketch, "E4.9.2.3", {"start": v(31, -39) * mm, "end": v(39, -39) * mm});
            skLineSegment(sketch, "E4.9.3.0", {"start": v(39, -29) * mm, "end": v(39, -21) * mm});
            skLineSegment(sketch, "E4.9.3.1", {"start": v(31, -29) * mm, "end": v(31, -21) * mm});
            skLineSegment(sketch, "E4.9.3.2", {"start": v(31, -21) * mm, "end": v(39, -21) * mm});
            skLineSegment(sketch, "E4.9.3.3", {"start": v(31, -29) * mm, "end": v(39, -29) * mm});
            skLineSegment(sketch, "E4.9.4.0", {"start": v(39, -19) * mm, "end": v(39, -11) * mm});
            skLineSegment(sketch, "E4.9.4.1", {"start": v(31, -19) * mm, "end": v(31, -11) * mm});
            skLineSegment(sketch, "E4.9.4.2", {"start": v(31, -11) * mm, "end": v(39, -11) * mm});
            skLineSegment(sketch, "E4.9.4.3", {"start": v(31, -19) * mm, "end": v(39, -19) * mm});
            skLineSegment(sketch, "E4.9.5.0", {"start": v(39, -9) * mm, "end": v(39, -1) * mm});
            skLineSegment(sketch, "E4.9.5.1", {"start": v(31, -9) * mm, "end": v(31, -1) * mm});
            skLineSegment(sketch, "E4.9.5.2", {"start": v(31, -1) * mm, "end": v(39, -1) * mm});
            skLineSegment(sketch, "E4.9.5.3", {"start": v(31, -9) * mm, "end": v(39, -9) * mm});
            skLineSegment(sketch, "E4.9.6.0", {"start": v(39, 1) * mm, "end": v(39, 9) * mm});
            skLineSegment(sketch, "E4.9.6.1", {"start": v(31, 1) * mm, "end": v(31, 9) * mm});
            skLineSegment(sketch, "E4.9.6.2", {"start": v(31, 9) * mm, "end": v(39, 9) * mm});
            skLineSegment(sketch, "E4.9.6.3", {"start": v(31, 1) * mm, "end": v(39, 1) * mm});
            skLineSegment(sketch, "E4.9.7.0", {"start": v(39, 11) * mm, "end": v(39, 19) * mm});
            skLineSegment(sketch, "E4.9.7.1", {"start": v(31, 11) * mm, "end": v(31, 19) * mm});
            skLineSegment(sketch, "E4.9.7.2", {"start": v(31, 19) * mm, "end": v(39, 19) * mm});
            skLineSegment(sketch, "E4.9.7.3", {"start": v(31, 11) * mm, "end": v(39, 11) * mm});
            skLineSegment(sketch, "E4.9.8.0", {"start": v(39, 21) * mm, "end": v(39, 29) * mm});
            skLineSegment(sketch, "E4.9.8.1", {"start": v(31, 21) * mm, "end": v(31, 29) * mm});
            skLineSegment(sketch, "E4.9.8.2", {"start": v(31, 29) * mm, "end": v(39, 29) * mm});
            skLineSegment(sketch, "E4.9.8.3", {"start": v(31, 21) * mm, "end": v(39, 21) * mm});
            skLineSegment(sketch, "E4.9.9.0", {"start": v(39, 31) * mm, "end": v(39, 39) * mm});
            skLineSegment(sketch, "E4.9.9.1", {"start": v(31, 31) * mm, "end": v(31, 39) * mm});
            skLineSegment(sketch, "E4.9.9.2", {"start": v(31, 39) * mm, "end": v(39, 39) * mm});
            skLineSegment(sketch, "E4.9.9.3", {"start": v(31, 31) * mm, "end": v(39, 31) * mm});
            skLineSegment(sketch, "E4.9.10.0", {"start": v(39, 41) * mm, "end": v(39, 49) * mm});
            skLineSegment(sketch, "E4.9.10.1", {"start": v(31, 41) * mm, "end": v(31, 49) * mm});
            skLineSegment(sketch, "E4.9.10.2", {"start": v(31, 49) * mm, "end": v(39, 49) * mm});
            skLineSegment(sketch, "E4.9.10.3", {"start": v(31, 41) * mm, "end": v(39, 41) * mm});
            skLineSegment(sketch, "E4.10.0.0", {"start": v(49, -59) * mm, "end": v(49, -51) * mm});
            skLineSegment(sketch, "E4.10.0.1", {"start": v(41, -59) * mm, "end": v(41, -51) * mm});
            skLineSegment(sketch, "E4.10.0.2", {"start": v(41, -51) * mm, "end": v(49, -51) * mm});
            skLineSegment(sketch, "E4.10.0.3", {"start": v(41, -59) * mm, "end": v(49, -59) * mm});
            skLineSegment(sketch, "E4.10.1.0", {"start": v(49, -49) * mm, "end": v(49, -41) * mm});
            skLineSegment(sketch, "E4.10.1.1", {"start": v(41, -49) * mm, "end": v(41, -41) * mm});
            skLineSegment(sketch, "E4.10.1.2", {"start": v(41, -41) * mm, "end": v(49, -41) * mm});
            skLineSegment(sketch, "E4.10.1.3", {"start": v(41, -49) * mm, "end": v(49, -49) * mm});
            skLineSegment(sketch, "E4.10.2.0", {"start": v(49, -39) * mm, "end": v(49, -31) * mm});
            skLineSegment(sketch, "E4.10.2.1", {"start": v(41, -39) * mm, "end": v(41, -31) * mm});
            skLineSegment(sketch, "E4.10.2.2", {"start": v(41, -31) * mm, "end": v(49, -31) * mm});
            skLineSegment(sketch, "E4.10.2.3", {"start": v(41, -39) * mm, "end": v(49, -39) * mm});
            skLineSegment(sketch, "E4.10.3.0", {"start": v(49, -29) * mm, "end": v(49, -21) * mm});
            skLineSegment(sketch, "E4.10.3.1", {"start": v(41, -29) * mm, "end": v(41, -21) * mm});
            skLineSegment(sketch, "E4.10.3.2", {"start": v(41, -21) * mm, "end": v(49, -21) * mm});
            skLineSegment(sketch, "E4.10.3.3", {"start": v(41, -29) * mm, "end": v(49, -29) * mm});
            skLineSegment(sketch, "E4.10.4.0", {"start": v(49, -19) * mm, "end": v(49, -11) * mm});
            skLineSegment(sketch, "E4.10.4.1", {"start": v(41, -19) * mm, "end": v(41, -11) * mm});
            skLineSegment(sketch, "E4.10.4.2", {"start": v(41, -11) * mm, "end": v(49, -11) * mm});
            skLineSegment(sketch, "E4.10.4.3", {"start": v(41, -19) * mm, "end": v(49, -19) * mm});
            skLineSegment(sketch, "E4.10.5.0", {"start": v(49, -9) * mm, "end": v(49, -1) * mm});
            skLineSegment(sketch, "E4.10.5.1", {"start": v(41, -9) * mm, "end": v(41, -1) * mm});
            skLineSegment(sketch, "E4.10.5.2", {"start": v(41, -1) * mm, "end": v(49, -1) * mm});
            skLineSegment(sketch, "E4.10.5.3", {"start": v(41, -9) * mm, "end": v(49, -9) * mm});
            skLineSegment(sketch, "E4.10.6.0", {"start": v(49, 1) * mm, "end": v(49, 9) * mm});
            skLineSegment(sketch, "E4.10.6.1", {"start": v(41, 1) * mm, "end": v(41, 9) * mm});
            skLineSegment(sketch, "E4.10.6.2", {"start": v(41, 9) * mm, "end": v(49, 9) * mm});
            skLineSegment(sketch, "E4.10.6.3", {"start": v(41, 1) * mm, "end": v(49, 1) * mm});
            skLineSegment(sketch, "E4.10.7.0", {"start": v(49, 11) * mm, "end": v(49, 19) * mm});
            skLineSegment(sketch, "E4.10.7.1", {"start": v(41, 11) * mm, "end": v(41, 19) * mm});
            skLineSegment(sketch, "E4.10.7.2", {"start": v(41, 19) * mm, "end": v(49, 19) * mm});
            skLineSegment(sketch, "E4.10.7.3", {"start": v(41, 11) * mm, "end": v(49, 11) * mm});
            skLineSegment(sketch, "E4.10.8.0", {"start": v(49, 21) * mm, "end": v(49, 29) * mm});
            skLineSegment(sketch, "E4.10.8.1", {"start": v(41, 21) * mm, "end": v(41, 29) * mm});
            skLineSegment(sketch, "E4.10.8.2", {"start": v(41, 29) * mm, "end": v(49, 29) * mm});
            skLineSegment(sketch, "E4.10.8.3", {"start": v(41, 21) * mm, "end": v(49, 21) * mm});
            skLineSegment(sketch, "E4.10.9.0", {"start": v(49, 31) * mm, "end": v(49, 39) * mm});
            skLineSegment(sketch, "E4.10.9.1", {"start": v(41, 31) * mm, "end": v(41, 39) * mm});
            skLineSegment(sketch, "E4.10.9.2", {"start": v(41, 39) * mm, "end": v(49, 39) * mm});
            skLineSegment(sketch, "E4.10.9.3", {"start": v(41, 31) * mm, "end": v(49, 31) * mm});
            skLineSegment(sketch, "E4.10.10.0", {"start": v(49, 41) * mm, "end": v(49, 49) * mm});
            skLineSegment(sketch, "E4.10.10.1", {"start": v(41, 41) * mm, "end": v(41, 49) * mm});
            skLineSegment(sketch, "E4.10.10.2", {"start": v(41, 49) * mm, "end": v(49, 49) * mm});
            skLineSegment(sketch, "E4.10.10.3", {"start": v(41, 41) * mm, "end": v(49, 41) * mm});
            skLineSegment(sketch, "E4.direction1", {"start": v(-59, -59) * mm, "end": v(-49, -59) * mm, "construction": true});
            skLineSegment(sketch, "E4.direction2", {"start": v(-59, -59) * mm, "end": v(-59, -49) * mm, "construction": true});
            skLineSegment(sketch, "E5.0.11.0", {"start": v(59, -59) * mm, "end": v(59, -51) * mm});
            skLineSegment(sketch, "E5.3.11.0", {"start": v(51, -59) * mm, "end": v(51, -51) * mm});
            skLineSegment(sketch, "E5.6.11.0", {"start": v(51, -51) * mm, "end": v(59, -51) * mm});
            skLineSegment(sketch, "E5.9.11.0", {"start": v(51, -59) * mm, "end": v(59, -59) * mm});
            skLineSegment(sketch, "E5.0.11.1", {"start": v(59, -49) * mm, "end": v(59, -41) * mm});
            skLineSegment(sketch, "E5.3.11.1", {"start": v(51, -49) * mm, "end": v(51, -41) * mm});
            skLineSegment(sketch, "E5.6.11.1", {"start": v(51, -41) * mm, "end": v(59, -41) * mm});
            skLineSegment(sketch, "E5.9.11.1", {"start": v(51, -49) * mm, "end": v(59, -49) * mm});
            skLineSegment(sketch, "E5.0.11.2", {"start": v(59, -39) * mm, "end": v(59, -31) * mm});
            skLineSegment(sketch, "E5.3.11.2", {"start": v(51, -39) * mm, "end": v(51, -31) * mm});
            skLineSegment(sketch, "E5.6.11.2", {"start": v(51, -31) * mm, "end": v(59, -31) * mm});
            skLineSegment(sketch, "E5.9.11.2", {"start": v(51, -39) * mm, "end": v(59, -39) * mm});
            skLineSegment(sketch, "E5.0.11.3", {"start": v(59, -29) * mm, "end": v(59, -21) * mm});
            skLineSegment(sketch, "E5.3.11.3", {"start": v(51, -29) * mm, "end": v(51, -21) * mm});
            skLineSegment(sketch, "E5.6.11.3", {"start": v(51, -21) * mm, "end": v(59, -21) * mm});
            skLineSegment(sketch, "E5.9.11.3", {"start": v(51, -29) * mm, "end": v(59, -29) * mm});
            skLineSegment(sketch, "E5.0.11.4", {"start": v(59, -19) * mm, "end": v(59, -11) * mm});
            skLineSegment(sketch, "E5.3.11.4", {"start": v(51, -19) * mm, "end": v(51, -11) * mm});
            skLineSegment(sketch, "E5.6.11.4", {"start": v(51, -11) * mm, "end": v(59, -11) * mm});
            skLineSegment(sketch, "E5.9.11.4", {"start": v(51, -19) * mm, "end": v(59, -19) * mm});
            skLineSegment(sketch, "E5.0.11.5", {"start": v(59, -9) * mm, "end": v(59, -1) * mm});
            skLineSegment(sketch, "E5.3.11.5", {"start": v(51, -9) * mm, "end": v(51, -1) * mm});
            skLineSegment(sketch, "E5.6.11.5", {"start": v(51, -1) * mm, "end": v(59, -1) * mm});
            skLineSegment(sketch, "E5.9.11.5", {"start": v(51, -9) * mm, "end": v(59, -9) * mm});
            skLineSegment(sketch, "E5.0.11.6", {"start": v(59, 1) * mm, "end": v(59, 9) * mm});
            skLineSegment(sketch, "E5.3.11.6", {"start": v(51, 1) * mm, "end": v(51, 9) * mm});
            skLineSegment(sketch, "E5.6.11.6", {"start": v(51, 9) * mm, "end": v(59, 9) * mm});
            skLineSegment(sketch, "E5.9.11.6", {"start": v(51, 1) * mm, "end": v(59, 1) * mm});
            skLineSegment(sketch, "E5.0.11.7", {"start": v(59, 11) * mm, "end": v(59, 19) * mm});
            skLineSegment(sketch, "E5.3.11.7", {"start": v(51, 11) * mm, "end": v(51, 19) * mm});
            skLineSegment(sketch, "E5.6.11.7", {"start": v(51, 19) * mm, "end": v(59, 19) * mm});
            skLineSegment(sketch, "E5.9.11.7", {"start": v(51, 11) * mm, "end": v(59, 11) * mm});
            skLineSegment(sketch, "E5.0.11.8", {"start": v(59, 21) * mm, "end": v(59, 29) * mm});
            skLineSegment(sketch, "E5.3.11.8", {"start": v(51, 21) * mm, "end": v(51, 29) * mm});
            skLineSegment(sketch, "E5.6.11.8", {"start": v(51, 29) * mm, "end": v(59, 29) * mm});
            skLineSegment(sketch, "E5.9.11.8", {"start": v(51, 21) * mm, "end": v(59, 21) * mm});
            skLineSegment(sketch, "E5.0.11.9", {"start": v(59, 31) * mm, "end": v(59, 39) * mm});
            skLineSegment(sketch, "E5.3.11.9", {"start": v(51, 31) * mm, "end": v(51, 39) * mm});
            skLineSegment(sketch, "E5.6.11.9", {"start": v(51, 39) * mm, "end": v(59, 39) * mm});
            skLineSegment(sketch, "E5.9.11.9", {"start": v(51, 31) * mm, "end": v(59, 31) * mm});
            skLineSegment(sketch, "E5.0.11.10", {"start": v(59, 41) * mm, "end": v(59, 49) * mm});
            skLineSegment(sketch, "E5.3.11.10", {"start": v(51, 41) * mm, "end": v(51, 49) * mm});
            skLineSegment(sketch, "E5.6.11.10", {"start": v(51, 49) * mm, "end": v(59, 49) * mm});
            skLineSegment(sketch, "E5.9.11.10", {"start": v(51, 41) * mm, "end": v(59, 41) * mm});
            skLineSegment(sketch, "E6.0.0.11", {"start": v(-51, 51) * mm, "end": v(-51, 59) * mm});
            skLineSegment(sketch, "E6.3.0.11", {"start": v(-59, 51) * mm, "end": v(-59, 59) * mm});
            skLineSegment(sketch, "E6.6.0.11", {"start": v(-59, 59) * mm, "end": v(-51, 59) * mm});
            skLineSegment(sketch, "E6.9.0.11", {"start": v(-59, 51) * mm, "end": v(-51, 51) * mm});
            skLineSegment(sketch, "E6.0.1.11", {"start": v(-41, 51) * mm, "end": v(-41, 59) * mm});
            skLineSegment(sketch, "E6.3.1.11", {"start": v(-49, 51) * mm, "end": v(-49, 59) * mm});
            skLineSegment(sketch, "E6.6.1.11", {"start": v(-49, 59) * mm, "end": v(-41, 59) * mm});
            skLineSegment(sketch, "E6.9.1.11", {"start": v(-49, 51) * mm, "end": v(-41, 51) * mm});
            skLineSegment(sketch, "E6.0.2.11", {"start": v(-31, 51) * mm, "end": v(-31, 59) * mm});
            skLineSegment(sketch, "E6.3.2.11", {"start": v(-39, 51) * mm, "end": v(-39, 59) * mm});
            skLineSegment(sketch, "E6.6.2.11", {"start": v(-39, 59) * mm, "end": v(-31, 59) * mm});
            skLineSegment(sketch, "E6.9.2.11", {"start": v(-39, 51) * mm, "end": v(-31, 51) * mm});
            skLineSegment(sketch, "E6.0.3.11", {"start": v(-21, 51) * mm, "end": v(-21, 59) * mm});
            skLineSegment(sketch, "E6.3.3.11", {"start": v(-29, 51) * mm, "end": v(-29, 59) * mm});
            skLineSegment(sketch, "E6.6.3.11", {"start": v(-29, 59) * mm, "end": v(-21, 59) * mm});
            skLineSegment(sketch, "E6.9.3.11", {"start": v(-29, 51) * mm, "end": v(-21, 51) * mm});
            skLineSegment(sketch, "E6.0.4.11", {"start": v(-11, 51) * mm, "end": v(-11, 59) * mm});
            skLineSegment(sketch, "E6.3.4.11", {"start": v(-19, 51) * mm, "end": v(-19, 59) * mm});
            skLineSegment(sketch, "E6.6.4.11", {"start": v(-19, 59) * mm, "end": v(-11, 59) * mm});
            skLineSegment(sketch, "E6.9.4.11", {"start": v(-19, 51) * mm, "end": v(-11, 51) * mm});
            skLineSegment(sketch, "E6.0.5.11", {"start": v(-1, 51) * mm, "end": v(-1, 59) * mm});
            skLineSegment(sketch, "E6.3.5.11", {"start": v(-9, 51) * mm, "end": v(-9, 59) * mm});
            skLineSegment(sketch, "E6.6.5.11", {"start": v(-9, 59) * mm, "end": v(-1, 59) * mm});
            skLineSegment(sketch, "E6.9.5.11", {"start": v(-9, 51) * mm, "end": v(-1, 51) * mm});
            skLineSegment(sketch, "E6.0.6.11", {"start": v(9, 51) * mm, "end": v(9, 59) * mm});
            skLineSegment(sketch, "E6.3.6.11", {"start": v(1, 51) * mm, "end": v(1, 59) * mm});
            skLineSegment(sketch, "E6.6.6.11", {"start": v(1, 59) * mm, "end": v(9, 59) * mm});
            skLineSegment(sketch, "E6.9.6.11", {"start": v(1, 51) * mm, "end": v(9, 51) * mm});
            skLineSegment(sketch, "E6.0.7.11", {"start": v(19, 51) * mm, "end": v(19, 59) * mm});
            skLineSegment(sketch, "E6.3.7.11", {"start": v(11, 51) * mm, "end": v(11, 59) * mm});
            skLineSegment(sketch, "E6.6.7.11", {"start": v(11, 59) * mm, "end": v(19, 59) * mm});
            skLineSegment(sketch, "E6.9.7.11", {"start": v(11, 51) * mm, "end": v(19, 51) * mm});
            skLineSegment(sketch, "E6.0.8.11", {"start": v(29, 51) * mm, "end": v(29, 59) * mm});
            skLineSegment(sketch, "E6.3.8.11", {"start": v(21, 51) * mm, "end": v(21, 59) * mm});
            skLineSegment(sketch, "E6.6.8.11", {"start": v(21, 59) * mm, "end": v(29, 59) * mm});
            skLineSegment(sketch, "E6.9.8.11", {"start": v(21, 51) * mm, "end": v(29, 51) * mm});
            skLineSegment(sketch, "E6.0.9.11", {"start": v(39, 51) * mm, "end": v(39, 59) * mm});
            skLineSegment(sketch, "E6.3.9.11", {"start": v(31, 51) * mm, "end": v(31, 59) * mm});
            skLineSegment(sketch, "E6.6.9.11", {"start": v(31, 59) * mm, "end": v(39, 59) * mm});
            skLineSegment(sketch, "E6.9.9.11", {"start": v(31, 51) * mm, "end": v(39, 51) * mm});
            skLineSegment(sketch, "E6.0.10.11", {"start": v(49, 51) * mm, "end": v(49, 59) * mm});
            skLineSegment(sketch, "E6.3.10.11", {"start": v(41, 51) * mm, "end": v(41, 59) * mm});
            skLineSegment(sketch, "E6.6.10.11", {"start": v(41, 59) * mm, "end": v(49, 59) * mm});
            skLineSegment(sketch, "E6.9.10.11", {"start": v(41, 51) * mm, "end": v(49, 51) * mm});
            skLineSegment(sketch, "E6.0.11.11", {"start": v(59, 51) * mm, "end": v(59, 59) * mm});
            skLineSegment(sketch, "E6.3.11.11", {"start": v(51, 51) * mm, "end": v(51, 59) * mm});
            skLineSegment(sketch, "E6.6.11.11", {"start": v(51, 59) * mm, "end": v(59, 59) * mm});
            skLineSegment(sketch, "E6.9.11.11", {"start": v(51, 51) * mm, "end": v(59, 51) * mm});
            skSolve(sketch);
        }
        {
            var Q0;
            Q0 = qSketchRegion(id + "F4", true);
            extrude(context, id + "F5", {"entities" : qUnion([Q0]), "operationType" : NewBodyOperationType.REMOVE, "oppositeDirection" : true, "depth" : 1 * mm});
        }
        {
            var Q0;
            Q0=makeQuery(id+"F4.imprint","IMPRINT",FACE,{"disambiguationData":[TD([[makeQuery(id+"F4.imprint","IMPRINT",EDGE,{"derivedFrom":sQuery(id+"F4.wireOp",EDGE,"E3.bottom")}),-1.0]])]});
            var sketch = newSketch(context, id + "F6", { "sketchPlane" : qUnion([Q0])});
            skLineSegment(sketch, "E7.bottom", {"start": v(-61, 1) * mm, "end": v(61, 1) * mm});
            skLineSegment(sketch, "E7.top", {"start": v(-61, -1) * mm, "end": v(61, -1) * mm});
            skLineSegment(sketch, "E7.left", {"start": v(-61, 1) * mm, "end": v(-61, -1) * mm});
            skLineSegment(sketch, "E7.right", {"start": v(61, 1) * mm, "end": v(61, -4.94) * mm});
            skPoint(sketch, "E7.middle", {"position": v(0, 0) * mm});
            skLineSegment(sketch, "E8.bottom", {"start": v(-1, 61) * mm, "end": v(1, 61) * mm});
            skLineSegment(sketch, "E8.top", {"start": v(-1, -61) * mm, "end": v(1, -61) * mm});
            skLineSegment(sketch, "E8.left", {"start": v(-1, 61) * mm, "end": v(-1, -61) * mm});
            skLineSegment(sketch, "E8.right", {"start": v(1, 61) * mm, "end": v(1, -61) * mm});
            skSolve(sketch);
        }
        {
            var Q0;
            Q0 = qSketchRegion(id + "F6", true);
            extrude(context, id + "F7", {"entities" : qUnion([Q0]), "operationType" : NewBodyOperationType.REMOVE, "oppositeDirection" : true, "depth" : 2 * mm, "offsetDistance" : 25 * mm});
        }
    });
